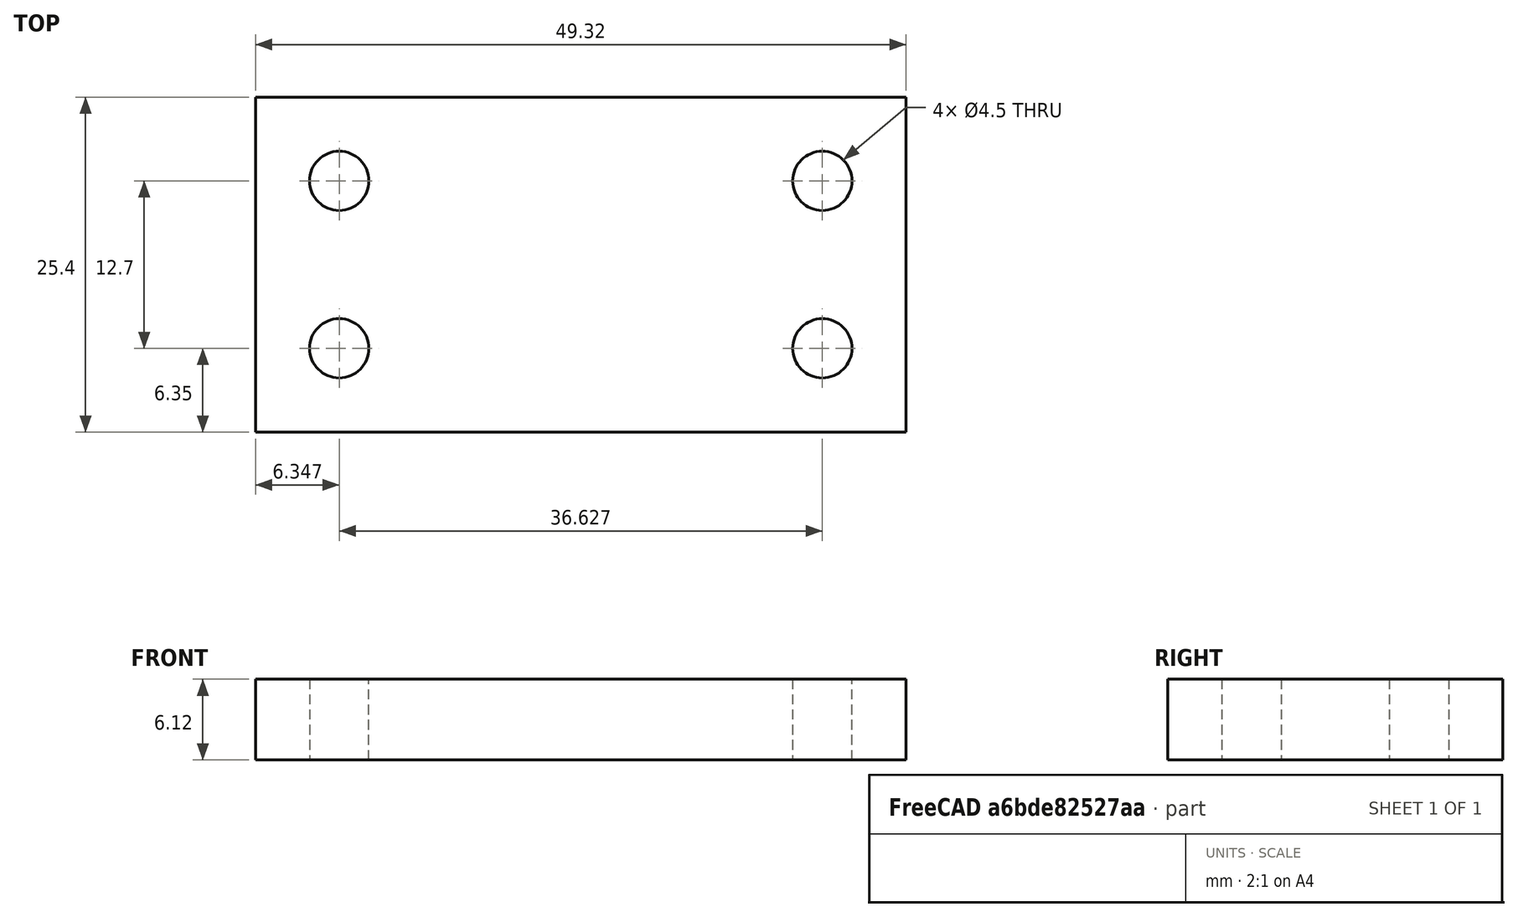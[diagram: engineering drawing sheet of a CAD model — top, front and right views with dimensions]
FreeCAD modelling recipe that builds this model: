
FCSTD DOCUMENT  (FreeCAD 0.17R13541 (Git))
Label: motor_spacer
License: All rights reserved
LicenseURL: http://en.wikipedia.org/wiki/All_rights_reserved
objects: Sketcher::SketchObject×1, PartDesign::Pad×1, PartDesign::Body×1
note: 4 computed .brp shape members not serialized (recipe doc carries the construction recipe); baked Part::Feature solids carry a one-line shape summary decoded from their .brp

FEATURE [Sketcher::SketchObject] Sketch
  MapMode = 5
  Support = -> [XY_Plane]
  sketch-geometry (12):
    g0: LineSegment StartX=-24.6634 StartY=12.7 StartZ=0 EndX=24.6634 EndY=12.7 EndZ=0
    g1: LineSegment StartX=24.6634 StartY=12.7 StartZ=0 EndX=24.6634 EndY=-12.7 EndZ=0
    g2: LineSegment StartX=24.6634 StartY=-12.7 StartZ=0 EndX=-24.6634 EndY=-12.7 EndZ=0
    g3: LineSegment StartX=-24.6634 StartY=-12.7 StartZ=0 EndX=-24.6634 EndY=12.7 EndZ=0
    g4: LineSegment [constr] StartX=-18.3134 StartY=6.35 StartZ=0 EndX=18.3134 EndY=6.35 EndZ=0
    g5: LineSegment [constr] StartX=18.3134 StartY=6.35 StartZ=0 EndX=18.3134 EndY=-6.35 EndZ=0
    g6: LineSegment [constr] StartX=18.3134 StartY=-6.35 StartZ=0 EndX=-18.3134 EndY=-6.35 EndZ=0
    g7: LineSegment [constr] StartX=-18.3134 StartY=-6.35 StartZ=0 EndX=-18.3134 EndY=6.35 EndZ=0
    g8: Circle CenterX=-18.3134 CenterY=6.35 CenterZ=0 NormalX=0 NormalY=0 NormalZ=1 AngleXU=0 Radius=2.2479
    g9: Circle CenterX=-18.3134 CenterY=-6.35 CenterZ=0 NormalX=0 NormalY=0 NormalZ=1 AngleXU=0 Radius=2.2479
    g10: Circle CenterX=18.3134 CenterY=-6.35 CenterZ=0 NormalX=0 NormalY=0 NormalZ=1 AngleXU=0 Radius=2.2479
    g11: Circle CenterX=18.3134 CenterY=6.35 CenterZ=0 NormalX=0 NormalY=0 NormalZ=1 AngleXU=0 Radius=2.2479
  constraints (31):
    c: Coincident(g0,g1)
    c: Coincident(g1,g2)
    c: Coincident(g2,g3)
    c: Coincident(g3,g0)
    c: Horizontal(g0)
    c: Horizontal(g2)
    c: Vertical(g1)
    c: Vertical(g3)
    c: DistanceX(g0,g0) = 49.3268
    c: DistanceY(g1,g1) = 25.4
    c: Symmetric(g0,g1,g-1)
    c: Coincident(g4,g5)
    c: Coincident(g5,g6)
    c: Coincident(g6,g7)
    c: Coincident(g7,g4)
    c: Horizontal(g4)
    c: Horizontal(g6)
    c: Vertical(g5)
    c: Vertical(g7)
    c: DistanceY(g4,g0) = 6.35
    c: DistanceY(g2,g6) = 6.35
    c: DistanceX(g2,g6) = 6.35
    c: DistanceX(g5,g1) = 6.35
    c: Coincident(g8,g4)
    c: Coincident(g9,g6)
    c: Coincident(g11,g4)
    c: Radius(g8) = 2.2479
    c: Equal(g8,g9)
    c: Equal(g8,g10)
    c: Equal(g8,g11)
    c: Coincident(g10,g5)
FEATURE [PartDesign::Pad] Pad
  Length = 6.1214
  Length2 = 99.9998
  Profile = -> Sketch
  Type = 0
FEATURE [PartDesign::Body] Body
  Group = -> [Sketch,Pad]
  Origin = -> Origin
  Tip = -> Pad
